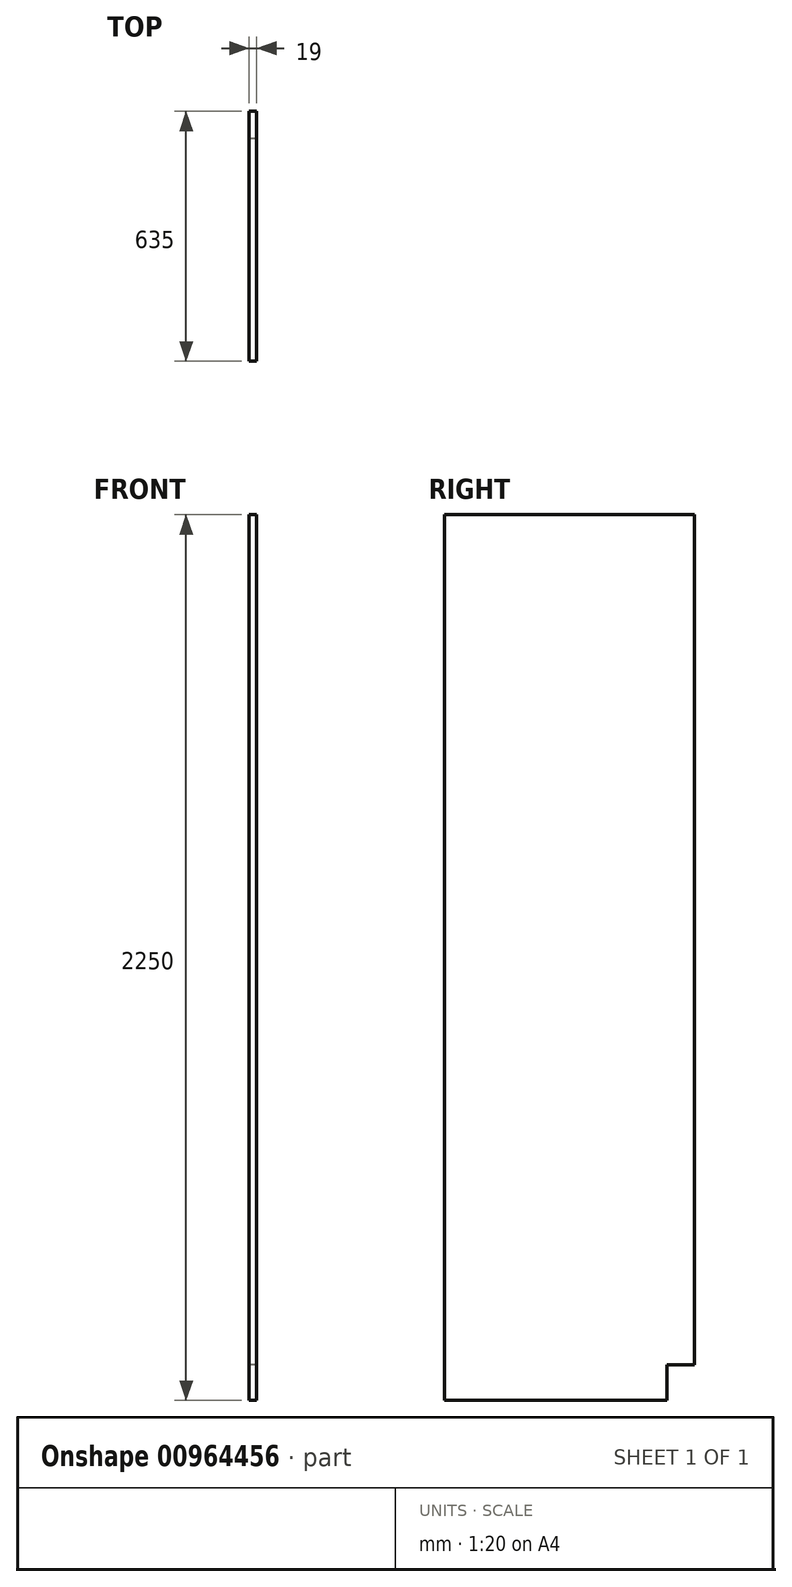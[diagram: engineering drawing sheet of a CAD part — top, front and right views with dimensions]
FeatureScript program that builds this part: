
annotation { "Feature Type Name" : "Feature", "Feature Type Description" : "" }
export const myFeature = defineFeature(function(context is Context, id is Id, definition is map)
    precondition{}
    {
        {
            var Q0;
            Q0=qCreatedBy(makeId("Right.planeOp"),FACE);
            var sketch = newSketch(context, id + "F0", { "sketchPlane" : qUnion([Q0])});
            skLineSegment(sketch, "E0.bottom", {"start": v(0, 0) * mm, "end": v(635, 0) * mm});
            skLineSegment(sketch, "E0.top", {"start": v(0, 2250) * mm, "end": v(635, 2250) * mm});
            skLineSegment(sketch, "E0.left", {"start": v(0, 0) * mm, "end": v(0, 2250) * mm});
            skLineSegment(sketch, "E0.right", {"start": v(635, 0) * mm, "end": v(635, 2250) * mm});
            skSolve(sketch);
        }
        {
            var Q0;
            Q0=makeQuery(id+"F0.imprint","IMPRINT",FACE,{"disambiguationData":[TD([[makeQuery(id+"F0.imprint","IMPRINT",EDGE,{"derivedFrom":sQuery(id+"F0.wireOp",EDGE,"E0.bottom")}),1.0]])]});
            extrude(context, id + "F1", {"entities" : qUnion([Q0]), "depth" : 19 * mm, "offsetDistance" : 25 * mm});
        }
        {
            var Q0;
            Q0=qCreatedBy(makeId("Right.planeOp"),FACE);
            var sketch = newSketch(context, id + "F2", { "sketchPlane" : qUnion([Q0])});
            skLineSegment(sketch, "E1.bottom", {"start": v(0, 0) * mm, "end": v(75, 0) * mm, "construction": true});
            skLineSegment(sketch, "E1.top", {"start": v(0, 90) * mm, "end": v(75, 90) * mm, "construction": true});
            skLineSegment(sketch, "E1.left", {"start": v(0, 0) * mm, "end": v(0, 90) * mm, "construction": true});
            skLineSegment(sketch, "E1.right", {"start": v(75, 0) * mm, "end": v(75, 90) * mm, "construction": true});
            skLineSegment(sketch, "E2.bottom", {"start": v(635, 0) * mm, "end": v(565, 0) * mm});
            skLineSegment(sketch, "E2.top", {"start": v(635, 90) * mm, "end": v(565, 90) * mm});
            skLineSegment(sketch, "E2.left", {"start": v(635, 0) * mm, "end": v(635, 90) * mm});
            skLineSegment(sketch, "E2.right", {"start": v(565, 0) * mm, "end": v(565, 90) * mm});
            skSolve(sketch);
        }
        {
            var Q0;
            Q0 = qSketchRegion(id + "F2", true);
            extrude(context, id + "F3", {"entities" : qUnion([Q0]), "operationType" : NewBodyOperationType.REMOVE, "endBound" : BoundingType.THROUGH_ALL, "depth" : 25 * mm, "offsetDistance" : 25 * mm});
        }
    });
